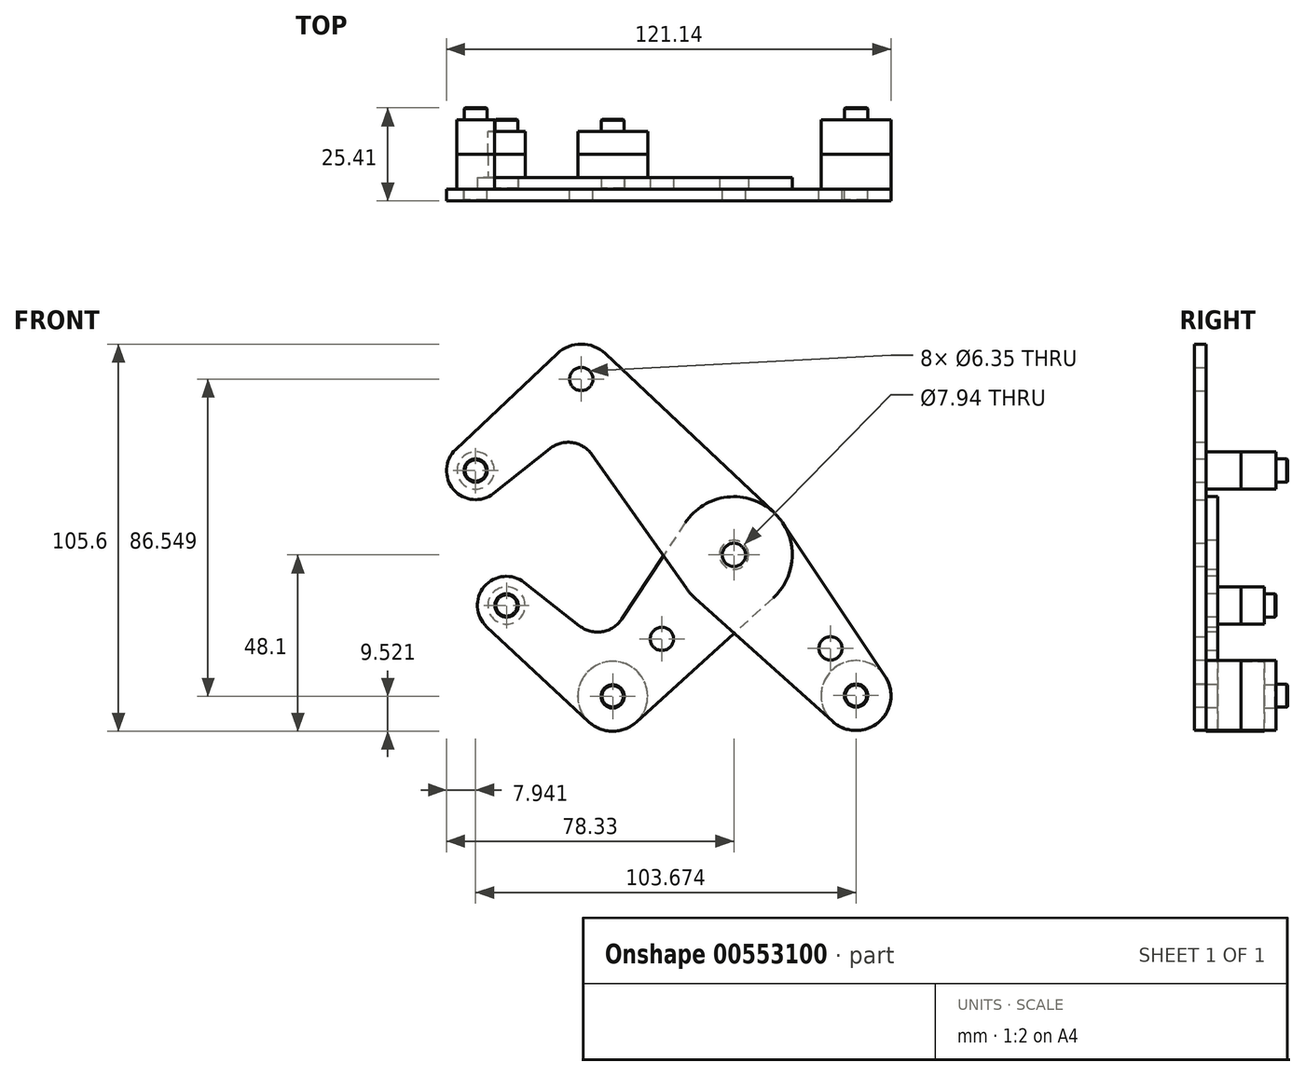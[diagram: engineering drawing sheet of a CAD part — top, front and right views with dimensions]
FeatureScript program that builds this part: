
annotation { "Feature Type Name" : "Feature", "Feature Type Description" : "" }
export const myFeature = defineFeature(function(context is Context, id is Id, definition is map)
    precondition{}
    {
        {
            var Q0;
            Q0=qCreatedBy(makeId("Front.planeOp"),FACE);
            var sketch = newSketch(context, id + "F0", { "sketchPlane" : qUnion([Q0])});
            skLineSegment(sketch, "E0", {"start": v(-41.6, 47.97) * mm, "end": v(41.6, -47.97) * mm, "construction": true});
            skCircle(sketch, "E1", {"center": v(0, 0) * mm, "radius": 3.18 * mm});
            skCircle(sketch, "E2", {"center": v(33.29, -38.38) * mm, "radius": 3.18 * mm});
            skCircle(sketch, "E3", {"center": v(-41.6, 47.97) * mm, "radius": 3.18 * mm});
            skCircle(sketch, "E4", {"center": v(-70.39, 23) * mm, "radius": 3.18 * mm});
            skLineSegment(sketch, "E5", {"start": v(-41.6, 47.97) * mm, "end": v(-70.39, 23) * mm, "construction": true});
            skCircle(sketch, "E6", {"center": v(33.29, -38.38) * mm, "radius": 9.53 * mm});
            skCircle(sketch, "E7", {"center": v(-70.39, 23) * mm, "radius": 7.94 * mm});
            skCircle(sketch, "E8", {"center": v(-41.6, 47.97) * mm, "radius": 9.53 * mm});
            skLineSegment(sketch, "E9", {"start": v(-75.83, 28.78) * mm, "end": v(-48.14, 54.9) * mm});
            skLineSegment(sketch, "E10", {"start": v(-65.44, 16.8) * mm, "end": v(-50.15, 28.98) * mm});
            skCircle(sketch, "E11", {"center": v(0, 0) * mm, "radius": 15.88 * mm});
            skLineSegment(sketch, "E12", {"start": v(-35.07, 54.9) * mm, "end": v(10.9, 11.55) * mm});
            skLineSegment(sketch, "E13", {"start": v(-38.72, 27.35) * mm, "end": v(-12.97, -9.15) * mm});
            skLineSegment(sketch, "E14", {"start": v(-10.6, -11.82) * mm, "end": v(26.93, -45.47) * mm});
            skLineSegment(sketch, "E15", {"start": v(13.2, 8.82) * mm, "end": v(41.2, -33.08) * mm});
            skArc(sketch, "E16.filletArc", {"start": v(-38.72, 27.35) * mm, "mid": v(-44.08, 30.63) * mm, "end": v(-50.15, 28.98) * mm});
            skLineSegment(sketch, "E17", {"start": v(0, 0) * mm, "end": v(-33.05, -38.58) * mm, "construction": true});
            skLineSegment(sketch, "E18", {"start": v(-33.05, -38.58) * mm, "end": v(-61.98, -13.8) * mm, "construction": true});
            skCircle(sketch, "E19", {"center": v(-61.98, -13.8) * mm, "radius": 3.18 * mm});
            skCircle(sketch, "E20", {"center": v(-33.05, -38.58) * mm, "radius": 3.18 * mm});
            skCircle(sketch, "E21", {"center": v(-61.98, -13.8) * mm, "radius": 7.94 * mm});
            skCircle(sketch, "E22", {"center": v(-33.05, -38.58) * mm, "radius": 9.53 * mm});
            skLineSegment(sketch, "E23", {"start": v(-57.08, -7.55) * mm, "end": v(-42.08, -19.35) * mm});
            skLineSegment(sketch, "E24", {"start": v(-67.4, -19.6) * mm, "end": v(-39.54, -45.55) * mm});
            skLineSegment(sketch, "E25", {"start": v(-13.25, 8.74) * mm, "end": v(-30.55, -17.48) * mm});
            skLineSegment(sketch, "E26", {"start": v(10.67, -11.75) * mm, "end": v(-26.65, -45.63) * mm});
            skArc(sketch, "E27.filletArc", {"start": v(-42.08, -19.35) * mm, "mid": v(-35.9, -20.95) * mm, "end": v(-30.55, -17.48) * mm});
            skCircle(sketch, "E28", {"center": v(-19.62, -22.9) * mm, "radius": 3.18 * mm});
            skCircle(sketch, "E29", {"center": v(26.32, -25.5) * mm, "radius": 3.18 * mm});
            skLineSegment(sketch, "E30", {"start": v(26.32, -25.5) * mm, "end": v(23.92, -27.58) * mm, "construction": true});
            skCircle(sketch, "E31", {"center": v(0, 0) * mm, "radius": 3.97 * mm});
            skSolve(sketch);
        }
        {
            var Q0;
            Q0=qCreatedBy(makeId("Front.planeOp"),FACE);
            cPlane(context, id + "F1", {"entities" : qUnion([Q0]), "cplaneType" : CPlaneType.OFFSET, "offset" : 9.52 * mm, "oppositeDirection" : true, "width" : 254 * mm, "height" : 254 * mm});
        }
        {
            var Q0;
            Q0=makeQuery(id+"F0.imprint","IMPRINT",FACE,{"disambiguationData":[TD([[makeQuery(id+"F0.imprint","IMPRINT",EDGE,{"derivedFrom":sQuery(id+"F0.wireOp",EDGE,"E2")}),-1.0]])]});
            var Q1;
            Q1=makeQuery(id+"F0.imprint","IMPRINT",FACE,{"disambiguationData":[TD([[makeQuery(id+"F0.imprint","IMPRINT",EDGE,{"derivedFrom":sQuery(id+"F0.wireOp",EDGE,"E3")}),-1.0]])]});
            var Q2;
            Q2=makeQuery(id+"F0.imprint","IMPRINT",FACE,{"disambiguationData":[TD([[makeQuery(id+"F0.imprint","IMPRINT",EDGE,{"derivedFrom":sQuery(id+"F0.wireOp",EDGE,"E4")}),-1.0]])]});
            var Q3;
            {var subQ0=sQuery(id+"F0.wireOp",EDGE,"E13");var subQ1=sQuery(id+"F0.wireOp",EDGE,"E11");var subQ2=makeQuery(id+"F0.imprint","INTERSECT",VERTEX,{"derivedFrom":[subQ1,subQ0]});Q3=makeQuery(id+"F0.imprint","IMPRINT",FACE,{"disambiguationData":[TD([[makeQuery(id+"F0.imprint","IMPRINT",EDGE,{"disambiguationData":[TD([[subQ2,1.0]])],"derivedFrom":subQ1}),-1.0]])]});}
            var Q4;
            {var subQ0=sQuery(id+"F0.wireOp",EDGE,"E14");var subQ1=sQuery(id+"F0.wireOp",EDGE,"E11");var subQ2=makeQuery(id+"F0.imprint","INTERSECT",VERTEX,{"derivedFrom":[subQ1,subQ0]});Q4=makeQuery(id+"F0.imprint","IMPRINT",FACE,{"disambiguationData":[TD([[makeQuery(id+"F0.imprint","IMPRINT",EDGE,{"disambiguationData":[TD([[subQ2,-1.0]])],"derivedFrom":subQ1}),-1.0]])]});}
            var Q5;
            {var subQ0=sQuery(id+"F0.wireOp",EDGE,"E15");Q5=makeQuery(id+"F0.imprint","IMPRINT",FACE,{"disambiguationData":[TD([[makeQuery(id+"F0.imprint","IMPRINT",EDGE,{"derivedFrom":subQ0}),-1.0]])]});}
            var Q6;
            Q6=makeQuery(id+"F0.imprint","IMPRINT",FACE,{"disambiguationData":[TD([[makeQuery(id+"F0.imprint","IMPRINT",EDGE,{"derivedFrom":sQuery(id+"F0.wireOp",EDGE,"E31")}),-1.0]])]});
            var Q7;
            {var subQ0=sQuery(id+"F0.wireOp",EDGE,"E9");Q7=makeQuery(id+"F0.imprint","IMPRINT",FACE,{"disambiguationData":[TD([[makeQuery(id+"F0.imprint","IMPRINT",EDGE,{"derivedFrom":subQ0}),-1.0]])]});}
            var Q8;
            Q8=makeQuery(id+"F0.imprint","IMPRINT",FACE,{"disambiguationData":[TD([[makeQuery(id+"F0.imprint","IMPRINT",EDGE,{"derivedFrom":sQuery(id+"F0.wireOp",EDGE,"E1")}),-1.0]])]});
            extrude(context, id + "F2", {"entities" : qUnion([Q0, Q1, Q2, Q3, Q4, Q5, Q6, Q7, Q8]), "depth" : 3.17 * mm});
        }
        {
            var Q0;
            Q0=makeQuery(id+"F0.imprint","IMPRINT",FACE,{"disambiguationData":[TD([[makeQuery(id+"F0.imprint","IMPRINT",EDGE,{"derivedFrom":sQuery(id+"F0.wireOp",EDGE,"E31")}),-1.0]])]});
            var Q1;
            {var subQ0=sQuery(id+"F0.wireOp",EDGE,"E13");var subQ1=sQuery(id+"F0.wireOp",EDGE,"E11");var subQ2=makeQuery(id+"F0.imprint","INTERSECT",VERTEX,{"derivedFrom":[subQ1,subQ0]});Q1=makeQuery(id+"F0.imprint","IMPRINT",FACE,{"disambiguationData":[TD([[makeQuery(id+"F0.imprint","IMPRINT",EDGE,{"disambiguationData":[TD([[subQ2,1.0]])],"derivedFrom":subQ1}),-1.0]])]});}
            var Q2;
            {var subQ0=sQuery(id+"F0.wireOp",EDGE,"E14");var subQ1=sQuery(id+"F0.wireOp",EDGE,"E11");var subQ2=makeQuery(id+"F0.imprint","INTERSECT",VERTEX,{"derivedFrom":[subQ1,subQ0]});Q2=makeQuery(id+"F0.imprint","IMPRINT",FACE,{"disambiguationData":[TD([[makeQuery(id+"F0.imprint","IMPRINT",EDGE,{"disambiguationData":[TD([[subQ2,-1.0]])],"derivedFrom":subQ1}),-1.0]])]});}
            var Q3;
            {var subQ13=sQuery(id+"F0.wireOp",EDGE,"E23");Q3=makeQuery(id+"F0.imprint","IMPRINT",FACE,{"disambiguationData":[TD([[makeQuery(id+"F0.imprint","IMPRINT",EDGE,{"derivedFrom":subQ13}),-1.0]])]});}
            var Q4;
            Q4=makeQuery(id+"F0.imprint","IMPRINT",FACE,{"disambiguationData":[TD([[makeQuery(id+"F0.imprint","IMPRINT",EDGE,{"derivedFrom":sQuery(id+"F0.wireOp",EDGE,"E20")}),-1.0]])]});
            var Q5;
            Q5=makeQuery(id+"F0.imprint","IMPRINT",FACE,{"disambiguationData":[TD([[makeQuery(id+"F0.imprint","IMPRINT",EDGE,{"derivedFrom":sQuery(id+"F0.wireOp",EDGE,"E19")}),-1.0]])]});
            extrude(context, id + "F3", {"entities" : qUnion([Q0, Q1, Q2, Q3, Q4, Q5]), "oppositeDirection" : true, "depth" : 3.17 * mm});
        }
        {
            var Q0;
            Q0=makeQuery(id+"F2.opExtrude","CAP_FACE",FACE,{"disambiguationData":[OSD([sQuery(id+"F0.wireOp",EDGE,"E1"),sQuery(id+"F0.wireOp",EDGE,"E2"),sQuery(id+"F0.wireOp",EDGE,"E3"),sQuery(id+"F0.wireOp",EDGE,"E4"),sQuery(id+"F0.wireOp",EDGE,"E6"),sQuery(id+"F0.wireOp",EDGE,"E7"),sQuery(id+"F0.wireOp",EDGE,"E8"),sQuery(id+"F0.wireOp",EDGE,"E9"),sQuery(id+"F0.wireOp",EDGE,"E10"),sQuery(id+"F0.wireOp",EDGE,"E11"),sQuery(id+"F0.wireOp",EDGE,"E12"),sQuery(id+"F0.wireOp",EDGE,"E13"),sQuery(id+"F0.wireOp",EDGE,"E14"),sQuery(id+"F0.wireOp",EDGE,"E15"),sQuery(id+"F0.wireOp",EDGE,"E16.filletArc"),sQuery(id+"F0.wireOp",EDGE,"E29")])],"isStart":false});
            var sketch = newSketch(context, id + "F4", { "sketchPlane" : qUnion([Q0])});
            skCircle(sketch, "E32", {"center": v(33.29, -38.38) * mm, "radius": 9.53 * mm});
            skCircle(sketch, "E33", {"center": v(-70.39, 23) * mm, "radius": 5.08 * mm});
            skSolve(sketch);
        }
        {
            var Q0;
            Q0=makeQuery(id+"F3.opExtrude","CAP_FACE",FACE,{"disambiguationData":[OSD([sQuery(id+"F0.wireOp",EDGE,"E11"),sQuery(id+"F0.wireOp",EDGE,"E19"),sQuery(id+"F0.wireOp",EDGE,"E20"),sQuery(id+"F0.wireOp",EDGE,"E21"),sQuery(id+"F0.wireOp",EDGE,"E22"),sQuery(id+"F0.wireOp",EDGE,"E23"),sQuery(id+"F0.wireOp",EDGE,"E24"),sQuery(id+"F0.wireOp",EDGE,"E25"),sQuery(id+"F0.wireOp",EDGE,"E26"),sQuery(id+"F0.wireOp",EDGE,"E27.filletArc"),sQuery(id+"F0.wireOp",EDGE,"E28"),sQuery(id+"F0.wireOp",EDGE,"E31")])],"isStart":true});
            var sketch = newSketch(context, id + "F5", { "sketchPlane" : qUnion([Q0])});
            skCircle(sketch, "E34", {"center": v(-33.05, -38.58) * mm, "radius": 9.53 * mm});
            skCircle(sketch, "E35", {"center": v(-61.98, -13.8) * mm, "radius": 5.08 * mm});
            skSolve(sketch);
        }
        {
            var Q0;
            Q0 = qSketchRegion(id + "F4", true);
            var Q1;
            Q1 = qSketchRegion(id + "F5", true);
            var Q2;
            Q2=qCreatedBy(id+"F1.planeOp",FACE);
            extrude(context, id + "F6", {"entities" : qUnion([Q0, Q1]), "endBound" : BoundingType.UP_TO_SURFACE, "oppositeDirection" : true, "endBoundEntityFace" : qUnion([Q2]), "depth" : 25.4 * mm});
        }
        {
            var Q0;
            Q0=makeQuery(id+"F2.opExtrude","SWEPT_BODY",BODY,{"disambiguationData":[OSD([sQuery(id+"F0.wireOp",EDGE,"E1"),sQuery(id+"F0.wireOp",EDGE,"E2"),sQuery(id+"F0.wireOp",EDGE,"E3"),sQuery(id+"F0.wireOp",EDGE,"E4"),sQuery(id+"F0.wireOp",EDGE,"E6"),sQuery(id+"F0.wireOp",EDGE,"E7"),sQuery(id+"F0.wireOp",EDGE,"E8"),sQuery(id+"F0.wireOp",EDGE,"E9"),sQuery(id+"F0.wireOp",EDGE,"E10"),sQuery(id+"F0.wireOp",EDGE,"E11"),sQuery(id+"F0.wireOp",EDGE,"E12"),sQuery(id+"F0.wireOp",EDGE,"E13"),sQuery(id+"F0.wireOp",EDGE,"E14"),sQuery(id+"F0.wireOp",EDGE,"E15"),sQuery(id+"F0.wireOp",EDGE,"E16.filletArc"),sQuery(id+"F0.wireOp",EDGE,"E29")])]});
            var Q1;
            Q1=makeQuery(id+"F3.opExtrude","SWEPT_BODY",BODY,{"disambiguationData":[OSD([sQuery(id+"F0.wireOp",EDGE,"E11"),sQuery(id+"F0.wireOp",EDGE,"E19"),sQuery(id+"F0.wireOp",EDGE,"E20"),sQuery(id+"F0.wireOp",EDGE,"E21"),sQuery(id+"F0.wireOp",EDGE,"E22"),sQuery(id+"F0.wireOp",EDGE,"E23"),sQuery(id+"F0.wireOp",EDGE,"E24"),sQuery(id+"F0.wireOp",EDGE,"E25"),sQuery(id+"F0.wireOp",EDGE,"E26"),sQuery(id+"F0.wireOp",EDGE,"E27.filletArc"),sQuery(id+"F0.wireOp",EDGE,"E28"),sQuery(id+"F0.wireOp",EDGE,"E31")])]});
            var Q2;
            Q2=makeQuery(id+"F6.opExtrude","SWEPT_BODY",BODY,{"disambiguationData":[OSD([sQuery(id+"F4.wireOp",EDGE,"E32")])]});
            var Q3;
            Q3=makeQuery(id+"F6.opExtrude","SWEPT_BODY",BODY,{"disambiguationData":[OSD([sQuery(id+"F5.wireOp",EDGE,"E34")])]});
            var Q4;
            Q4=makeQuery(id+"F6.opExtrude","SWEPT_BODY",BODY,{"disambiguationData":[OSD([sQuery(id+"F5.wireOp",EDGE,"E35")])]});
            var Q5;
            Q5=makeQuery(id+"F6.opExtrude","SWEPT_BODY",BODY,{"disambiguationData":[OSD([sQuery(id+"F4.wireOp",EDGE,"E33")])]});
            booleanBodies(context, id + "F7", {"operationType" : BooleanOperationType.SUBTRACTION, "tools" : qUnion([Q0, Q1]), "targets" : qUnion([Q2, Q3, Q4, Q5]), "offset" : true, "offsetAll" : true, "offsetDistance" : 0.03 * mm, "keepTools" : true});
        }
        {
            var Q0;
            Q0=makeQuery(id+"F9.opPattern","COPY",FACE,{"derivedFrom":makeQuery(id+"F6.opExtrude","CAP_FACE",FACE,{"disambiguationData":[OSD([sQuery(id+"F4.wireOp",EDGE,"E32")])],"isStart":true}),"instanceName":"1"});
            var Q1;
            Q1=makeQuery(id+"F9.opPattern","COPY",FACE,{"derivedFrom":makeQuery(id+"F6.opExtrude","CAP_FACE",FACE,{"disambiguationData":[OSD([sQuery(id+"F5.wireOp",EDGE,"E34")])],"isStart":true}),"instanceName":"1"});
            var Q2;
            Q2=makeQuery(id+"F9.opPattern","COPY",FACE,{"derivedFrom":makeQuery(id+"F6.opExtrude","CAP_FACE",FACE,{"disambiguationData":[OSD([sQuery(id+"F5.wireOp",EDGE,"E35")])],"isStart":true}),"instanceName":"1"});
            var Q3;
            Q3=makeQuery(id+"F9.opPattern","COPY",FACE,{"derivedFrom":makeQuery(id+"F6.opExtrude","CAP_FACE",FACE,{"disambiguationData":[OSD([sQuery(id+"F4.wireOp",EDGE,"E33")])],"isStart":true}),"instanceName":"1"});
            var Q4;
            Q4=makeQuery(id+"F6.opExtrude","CAP_FACE",FACE,{"disambiguationData":[OSD([sQuery(id+"F4.wireOp",EDGE,"E32")])],"isStart":true});
            var Q5;
            Q5=makeQuery(id+"F6.opExtrude","CAP_FACE",FACE,{"disambiguationData":[OSD([sQuery(id+"F5.wireOp",EDGE,"E34")])],"isStart":true});
            var Q6;
            Q6=makeQuery(id+"F6.opExtrude","CAP_FACE",FACE,{"disambiguationData":[OSD([sQuery(id+"F5.wireOp",EDGE,"E35")])],"isStart":true});
            var Q7;
            Q7=makeQuery(id+"F6.opExtrude","CAP_FACE",FACE,{"disambiguationData":[OSD([sQuery(id+"F4.wireOp",EDGE,"E33")])],"isStart":true});
            chamfer(context, id + "F8", {"entities" : qUnion([Q0, Q1, Q2, Q3, Q4, Q5, Q6, Q7]), "width" : 0.25 * mm});
        }
        {
            var Q0;
            Q0=makeQuery(id+"F6.opExtrude","SWEPT_BODY",BODY,{"disambiguationData":[OSD([sQuery(id+"F5.wireOp",EDGE,"E35")])]});
            var Q1;
            Q1=makeQuery(id+"F6.opExtrude","SWEPT_BODY",BODY,{"disambiguationData":[OSD([sQuery(id+"F5.wireOp",EDGE,"E34")])]});
            var Q2;
            Q2=makeQuery(id+"F6.opExtrude","SWEPT_BODY",BODY,{"disambiguationData":[OSD([sQuery(id+"F4.wireOp",EDGE,"E33")])]});
            var Q3;
            Q3=makeQuery(id+"F6.opExtrude","SWEPT_BODY",BODY,{"disambiguationData":[OSD([sQuery(id+"F4.wireOp",EDGE,"E32")])]});
            var Q4;
            Q4=qCreatedBy(id+"F1.planeOp",FACE);
            mirror(context, id + "F9", {"operationType" : NewBodyOperationType.ADD, "entities" : qUnion([Q0, Q1, Q2, Q3]), "mirrorPlane" : qUnion([Q4])});
        }
    });
